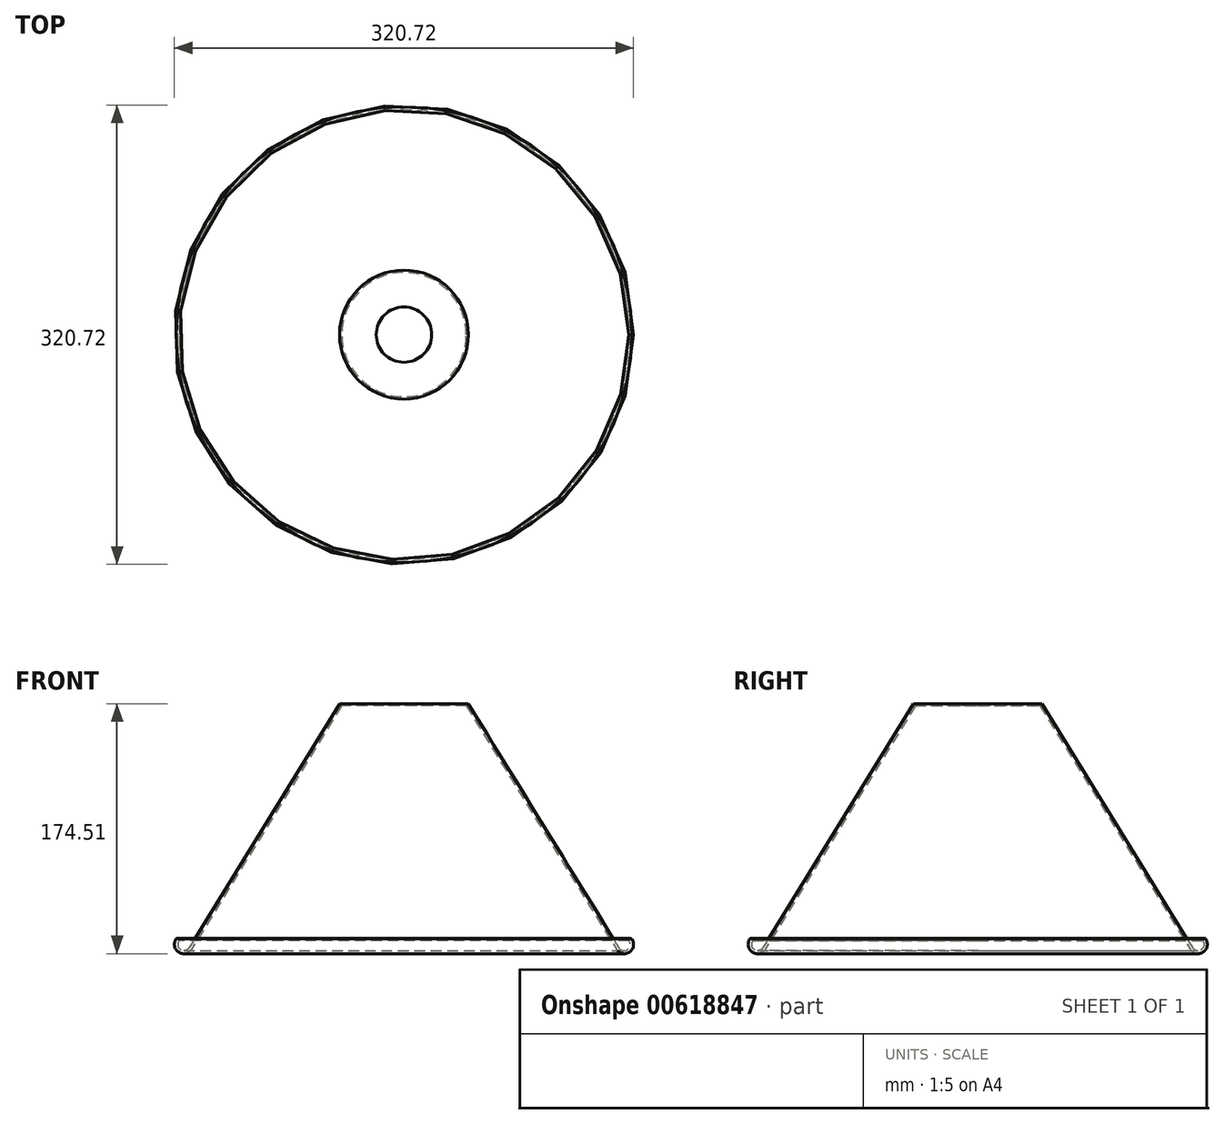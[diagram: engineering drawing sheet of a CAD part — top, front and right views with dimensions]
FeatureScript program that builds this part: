
annotation { "Feature Type Name" : "Feature", "Feature Type Description" : "" }
export const myFeature = defineFeature(function(context is Context, id is Id, definition is map)
    precondition{}
    {
        {
            var Q0;
            Q0=qCreatedBy(makeId("Front.planeOp"),FACE);
            var sketch = newSketch(context, id + "F0", { "sketchPlane" : qUnion([Q0])});
            skLineSegment(sketch, "E0", {"start": v(-19.34, 78.09) * mm, "end": v(-45, 78.01) * mm});
            skLineSegment(sketch, "E1", {"start": v(-19.34, 76.68) * mm, "end": v(-43.47, 76.68) * mm});
            skLineSegment(sketch, "E2", {"start": v(-45, 78.01) * mm, "end": v(-150.09, -92.3) * mm});
            skLineSegment(sketch, "E3", {"start": v(-148.38, -93.35) * mm, "end": v(-43.47, 76.68) * mm});
            skLineSegment(sketch, "E4", {"start": v(-19.34, 78.09) * mm, "end": v(-19.34, 76.68) * mm});
            skArc(sketch, "E5", {"start": v(-157.17, -87.45) * mm, "mid": v(-156.17, -93.58) * mm, "end": v(-150.09, -92.3) * mm});
            skArc(sketch, "E6", {"start": v(-159.1, -86.12) * mm, "mid": v(-157.5, -95.31) * mm, "end": v(-148.38, -93.35) * mm});
            skArc(sketch, "E7", {"start": v(-157.17, -87.45) * mm, "mid": v(-157.48, -85.83) * mm, "end": v(-159.1, -86.12) * mm});
            skSolve(sketch);
        }
        {
            var Q0;
            Q0=qCreatedBy(makeId("Front.planeOp"),FACE);
            var sketch = newSketch(context, id + "F1", { "sketchPlane" : qUnion([Q0])});
            skLineSegment(sketch, "E8", {"start": v(0, 88.37) * mm, "end": v(0, -131.63) * mm});
            skSolve(sketch);
        }
        {
            var Q0;
            Q0 = qSketchRegion(id + "F0", true);
            var Q1;
            Q1=sQuery(id+"F1.wireOp",EDGE,"E8");
            revolve(context, id + "F2", {"entities" : qUnion([Q0]), "axis" : qUnion([Q1]), "revolveType" : RevolveType.FULL});
        }
    });
